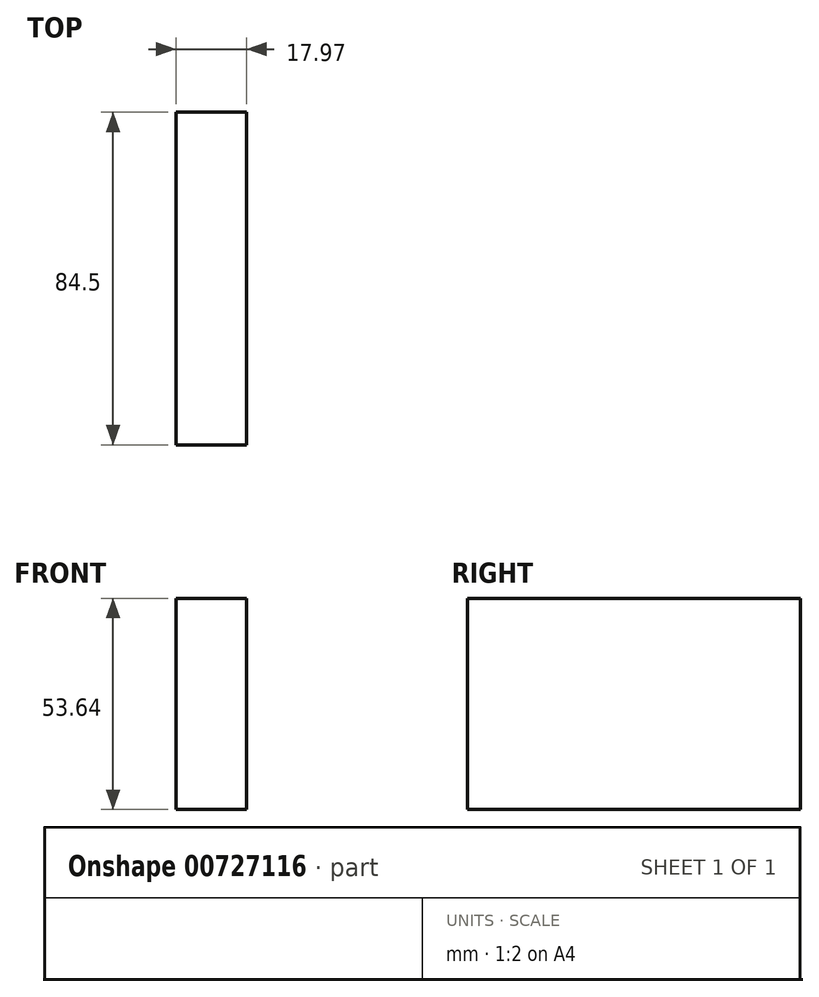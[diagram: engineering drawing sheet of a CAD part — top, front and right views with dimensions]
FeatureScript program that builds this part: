
annotation { "Feature Type Name" : "Feature", "Feature Type Description" : "" }
export const myFeature = defineFeature(function(context is Context, id is Id, definition is map)
    precondition{}
    {
        {
            var Q0;
            Q0=qCreatedBy(makeId("Front.planeOp"),FACE);
            var sketch = newSketch(context, id + "F0", { "sketchPlane" : qUnion([Q0])});
            skLineSegment(sketch, "E0.bottom", {"start": v(-7.9, -42.79) * mm, "end": v(10.07, -42.79) * mm});
            skLineSegment(sketch, "E0.top", {"start": v(-7.9, 10.85) * mm, "end": v(10.07, 10.85) * mm});
            skLineSegment(sketch, "E0.left", {"start": v(-7.9, -42.79) * mm, "end": v(-7.9, 10.85) * mm});
            skLineSegment(sketch, "E0.right", {"start": v(10.07, -42.79) * mm, "end": v(10.07, 10.85) * mm});
            skSolve(sketch);
        }
        {
            var Q0;
            Q0=makeQuery(id+"F0.imprint","IMPRINT",FACE,{"disambiguationData":[TD([[makeQuery(id+"F0.imprint","IMPRINT",EDGE,{"derivedFrom":sQuery(id+"F0.wireOp",EDGE,"E0.bottom")}),1.0]])]});
            extrude(context, id + "F1", {"entities" : qUnion([Q0]), "depth" : 84.5 * mm, "offsetDistance" : 25.4 * mm});
        }
    });
